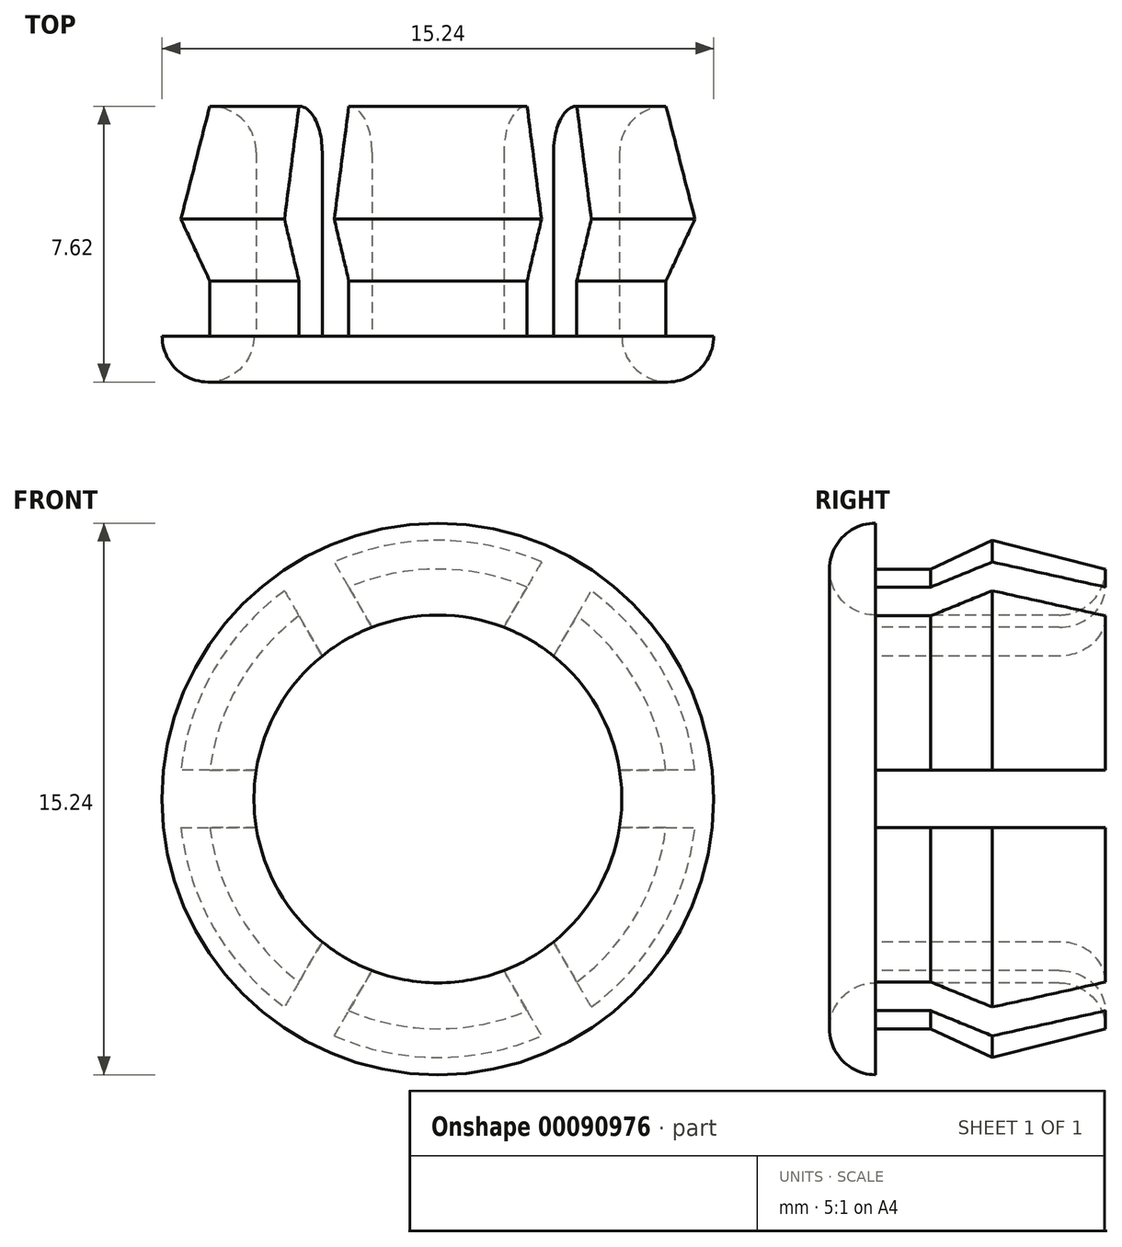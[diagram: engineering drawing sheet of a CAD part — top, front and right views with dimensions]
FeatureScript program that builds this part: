
annotation { "Feature Type Name" : "Feature", "Feature Type Description" : "" }
export const myFeature = defineFeature(function(context is Context, id is Id, definition is map)
    precondition{}
    {
        {
            var Q0;
            Q0=qCreatedBy(makeId("Top.planeOp"),FACE);
            var sketch = newSketch(context, id + "F0", { "sketchPlane" : qUnion([Q0])});
            skLineSegment(sketch, "E0", {"start": v(0, 0) * mm, "end": v(0, 6.35) * mm, "construction": true});
            skLineSegment(sketch, "E1", {"start": v(6.35, 0) * mm, "end": v(6.35, 1.52) * mm});
            skLineSegment(sketch, "E2", {"start": v(6.35, 1.52) * mm, "end": v(7.14, 3.23) * mm});
            skLineSegment(sketch, "E3", {"start": v(7.14, 3.23) * mm, "end": v(6.35, 6.35) * mm});
            skArc(sketch, "E4", {"start": v(6.35, 6.35) * mm, "mid": v(5.45, 5.98) * mm, "end": v(5.08, 5.08) * mm});
            skLineSegment(sketch, "E5", {"start": v(5.08, 5.08) * mm, "end": v(5.08, 0) * mm});
            skArc(sketch, "E6", {"start": v(5.08, 0) * mm, "mid": v(6.35, -1.27) * mm, "end": v(7.62, 0) * mm});
            skLineSegment(sketch, "E7", {"start": v(7.62, 0) * mm, "end": v(6.35, 0) * mm});
            skSolve(sketch);
        }
        {
            var Q0;
            Q0=makeQuery(id+"F0.imprint","IMPRINT",FACE,{"disambiguationData":[TD([[makeQuery(id+"F0.imprint","IMPRINT",EDGE,{"derivedFrom":sQuery(id+"F0.wireOp",EDGE,"E1")}),1.0]])]});
            var Q1;
            Q1=sQuery(id+"F0.wireOp",EDGE,"E0");
            revolve(context, id + "F1", {"entities" : qUnion([Q0]), "axis" : qUnion([Q1]), "revolveType" : RevolveType.FULL});
        }
        {
            var Q0;
            Q0=qCreatedBy(makeId("Front.planeOp"),FACE);
            var sketch = newSketch(context, id + "F2", { "sketchPlane" : qUnion([Q0])});
            skLineSegment(sketch, "E8", {"start": v(0, 0.8) * mm, "end": v(0, -0.8) * mm});
            skLineSegment(sketch, "E9", {"start": v(0, 0.8) * mm, "end": v(-12.7, 0.8) * mm});
            skLineSegment(sketch, "E10", {"start": v(-12.7, 0.8) * mm, "end": v(-12.7, -0.8) * mm});
            skLineSegment(sketch, "E11", {"start": v(-12.7, -0.8) * mm, "end": v(0, -0.8) * mm});
            skLineSegment(sketch, "E12.1.0", {"start": v(-0.69, 0.4) * mm, "end": v(-7.04, -10.6) * mm});
            skLineSegment(sketch, "E12.1.1", {"start": v(-7.04, -10.6) * mm, "end": v(-5.66, -11.4) * mm});
            skLineSegment(sketch, "E12.1.2", {"start": v(-5.66, -11.4) * mm, "end": v(0.69, -0.4) * mm});
            skLineSegment(sketch, "E12.1.3", {"start": v(-0.69, 0.4) * mm, "end": v(0.69, -0.4) * mm});
            skLineSegment(sketch, "E12.2.0", {"start": v(-0.69, -0.4) * mm, "end": v(5.66, -11.4) * mm});
            skLineSegment(sketch, "E12.2.1", {"start": v(5.66, -11.4) * mm, "end": v(7.04, -10.6) * mm});
            skLineSegment(sketch, "E12.2.2", {"start": v(7.04, -10.6) * mm, "end": v(0.69, 0.4) * mm});
            skLineSegment(sketch, "E12.2.3", {"start": v(-0.69, -0.4) * mm, "end": v(0.69, 0.4) * mm});
            skLineSegment(sketch, "E12.3.0", {"start": v(0, -0.8) * mm, "end": v(12.7, -0.8) * mm});
            skLineSegment(sketch, "E12.3.1", {"start": v(12.7, -0.8) * mm, "end": v(12.7, 0.8) * mm});
            skLineSegment(sketch, "E12.3.2", {"start": v(12.7, 0.8) * mm, "end": v(0, 0.8) * mm});
            skLineSegment(sketch, "E12.3.3", {"start": v(0, -0.8) * mm, "end": v(0, 0.8) * mm});
            skLineSegment(sketch, "E12.4.0", {"start": v(0.69, -0.4) * mm, "end": v(7.04, 10.6) * mm});
            skLineSegment(sketch, "E12.4.1", {"start": v(7.04, 10.6) * mm, "end": v(5.66, 11.4) * mm});
            skLineSegment(sketch, "E12.4.2", {"start": v(5.66, 11.4) * mm, "end": v(-0.69, 0.4) * mm});
            skLineSegment(sketch, "E12.4.3", {"start": v(0.69, -0.4) * mm, "end": v(-0.69, 0.4) * mm});
            skLineSegment(sketch, "E12.5.0", {"start": v(0.69, 0.4) * mm, "end": v(-5.66, 11.4) * mm});
            skLineSegment(sketch, "E12.5.1", {"start": v(-5.66, 11.4) * mm, "end": v(-7.04, 10.6) * mm});
            skLineSegment(sketch, "E12.5.2", {"start": v(-7.04, 10.6) * mm, "end": v(-0.69, -0.4) * mm});
            skLineSegment(sketch, "E12.5.3", {"start": v(0.69, 0.4) * mm, "end": v(-0.69, -0.4) * mm});
            skPoint(sketch, "E12.center", {"position": v(0, 0) * mm});
            skSolve(sketch);
        }
        {
            var Q0;
            Q0 = qSketchRegion(id + "F2", true);
            extrude(context, id + "F3", {"entities" : qUnion([Q0]), "operationType" : NewBodyOperationType.REMOVE, "endBound" : BoundingType.THROUGH_ALL, "oppositeDirection" : true, "depth" : 25 * mm});
        }
    });
